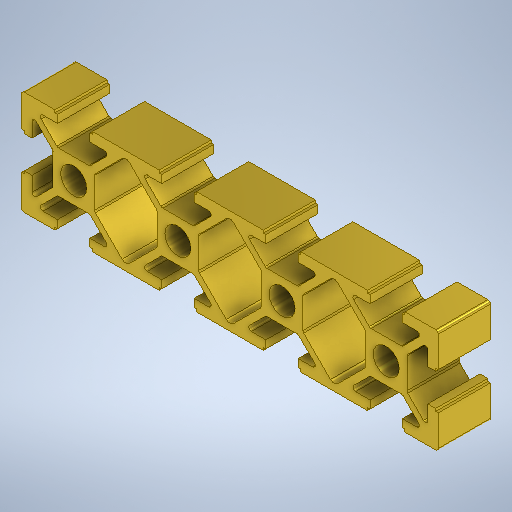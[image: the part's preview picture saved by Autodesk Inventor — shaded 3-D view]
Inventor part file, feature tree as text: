
AUTODESK INVENTOR PART (.ipt)
format: ipt  version: 2025.2 (Build 292293000, 293)  size: 580,608 bytes
history: native  units: mm
features: mirror x2, extrude x1, fillet x1, sketch x1
ambient origin geometry x8: Origin, YZ Plane, XZ Plane, XY Plane, X Axis, Y Axis, Z Axis, Center Point
bodies: Body1 (feature_tree)
feature tree (5):
  extrude  "Extrusão3"  Depth=10.0mm
  mirror  "Espelhar7"
  mirror  "Espelhar8"
  fillet  "Arredondamento5"  Radius=20.0mm
  sketch  "Esboço3"  dims[d45=80.0mm d46=10.0mm d47=20.0mm d48=6.2mm d49=5.0mm d51=6.0mm d54=0.5mm d56=2.0mm d57=0.5mm d59=4.0mm d67=1.5mm d68=10.0mm d69=0.0mm d70=1.0mm]
